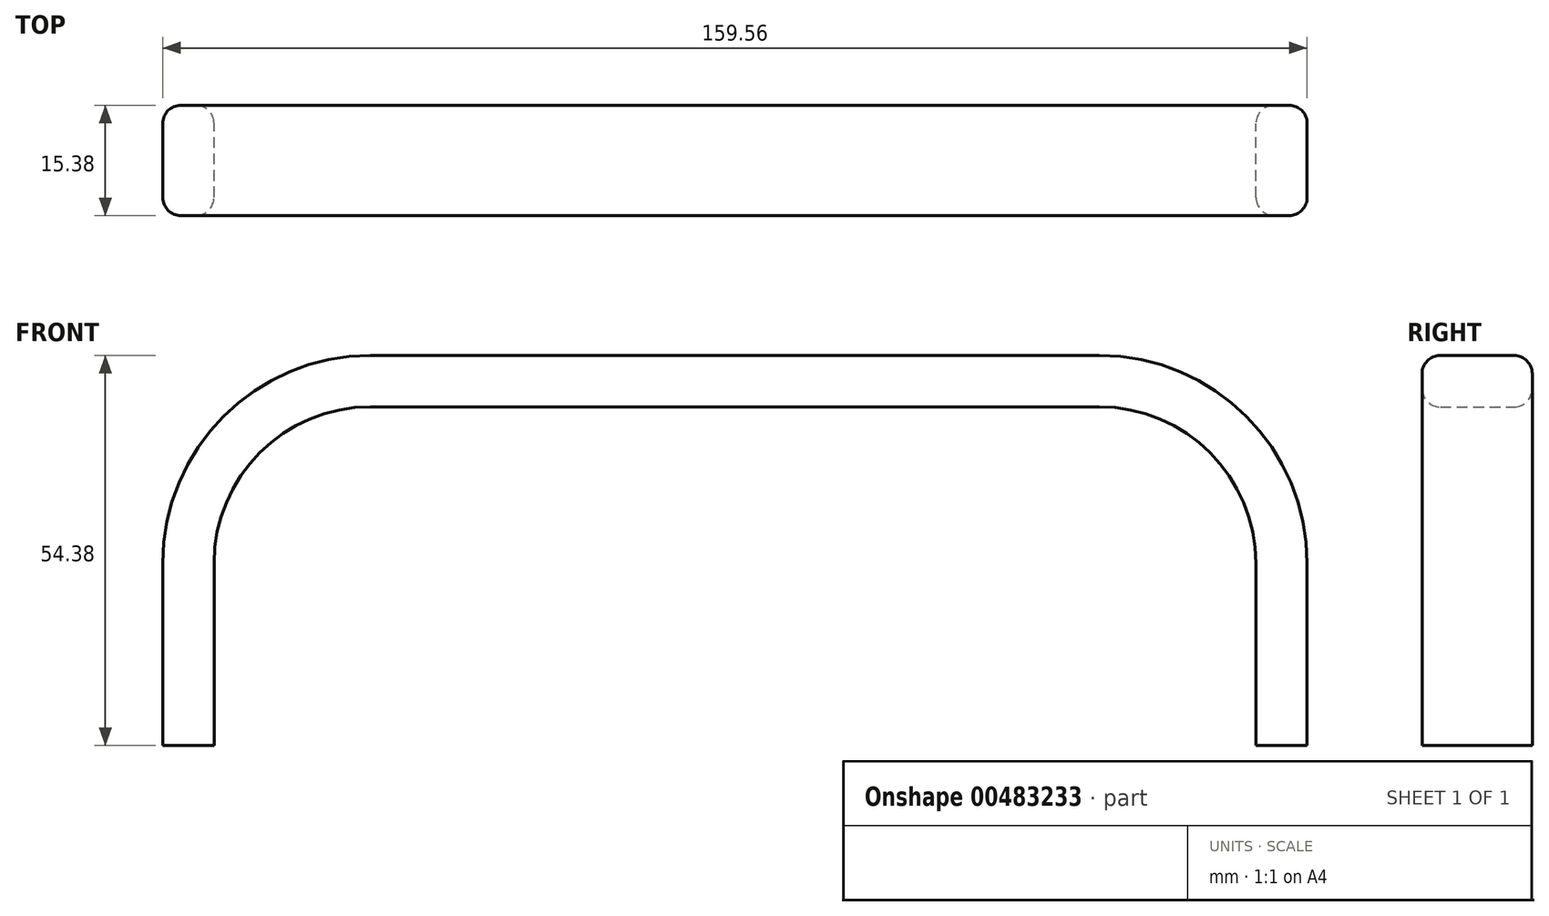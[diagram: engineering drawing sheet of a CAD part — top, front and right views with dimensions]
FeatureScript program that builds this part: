
annotation { "Feature Type Name" : "Feature", "Feature Type Description" : "" }
export const myFeature = defineFeature(function(context is Context, id is Id, definition is map)
    precondition{}
    {
        {
            var Q0;
            Q0=qCreatedBy(makeId("Front.planeOp"),FACE);
            var sketch = newSketch(context, id + "F0", { "sketchPlane" : qUnion([Q0])});
            skLineSegment(sketch, "E0", {"start": v(-76.2, 0) * mm, "end": v(-76.2, 25.4) * mm});
            skLineSegment(sketch, "E1", {"start": v(-50.8, 50.8) * mm, "end": v(50.8, 50.8) * mm});
            skLineSegment(sketch, "E2", {"start": v(76.2, 25.4) * mm, "end": v(76.2, 0) * mm});
            skPoint(sketch, "E3.visualSharp", {"position": v(-76.2, 50.8) * mm});
            skArc(sketch, "E3.filletArc", {"start": v(-50.8, 50.8) * mm, "mid": v(-68.76, 43.36) * mm, "end": v(-76.2, 25.4) * mm});
            skPoint(sketch, "E4.visualSharp", {"position": v(76.2, 50.8) * mm});
            skArc(sketch, "E4.filletArc", {"start": v(76.2, 25.4) * mm, "mid": v(68.76, 43.36) * mm, "end": v(50.8, 50.8) * mm});
            skSolve(sketch);
        }
        {
            var Q0;
            Q0=qCreatedBy(makeId("Top.planeOp"),FACE);
            var sketch = newSketch(context, id + "F1", { "sketchPlane" : qUnion([Q0])});
            skLineSegment(sketch, "E5.bottom", {"start": v(-75.16, -7.69) * mm, "end": v(-77.24, -7.69) * mm});
            skLineSegment(sketch, "E5.top", {"start": v(-75.16, 7.69) * mm, "end": v(-77.24, 7.69) * mm});
            skLineSegment(sketch, "E5.left", {"start": v(-72.62, -5.15) * mm, "end": v(-72.62, 5.15) * mm});
            skLineSegment(sketch, "E5.right", {"start": v(-79.78, -5.15) * mm, "end": v(-79.78, 5.15) * mm});
            skPoint(sketch, "E5.middle", {"position": v(-76.2, 0) * mm});
            skPoint(sketch, "E6.visualSharp", {"position": v(-79.78, -7.69) * mm});
            skArc(sketch, "E6.filletArc", {"start": v(-79.78, -5.15) * mm, "mid": v(-79.04, -6.94) * mm, "end": v(-77.24, -7.69) * mm});
            skPoint(sketch, "E7.visualSharp", {"position": v(-72.62, -7.69) * mm});
            skArc(sketch, "E7.filletArc", {"start": v(-75.16, -7.69) * mm, "mid": v(-73.36, -6.94) * mm, "end": v(-72.62, -5.15) * mm});
            skPoint(sketch, "E8.visualSharp", {"position": v(-72.62, 7.69) * mm});
            skArc(sketch, "E8.filletArc", {"start": v(-72.62, 5.15) * mm, "mid": v(-73.36, 6.94) * mm, "end": v(-75.16, 7.69) * mm});
            skPoint(sketch, "E9.visualSharp", {"position": v(-79.78, 7.69) * mm});
            skArc(sketch, "E9.filletArc", {"start": v(-77.24, 7.69) * mm, "mid": v(-79.04, 6.94) * mm, "end": v(-79.78, 5.15) * mm});
            skSolve(sketch);
        }
        {
            var Q0;
            Q0 = qSketchRegion(id + "F1", true);
            var Q1;
            Q1=sQuery(id+"F0.wireOp",EDGE,"E0");
            var Q2;
            Q2=sQuery(id+"F0.wireOp",EDGE,"E3.filletArc");
            var Q3;
            Q3=sQuery(id+"F0.wireOp",EDGE,"E1");
            var Q4;
            Q4=sQuery(id+"F0.wireOp",EDGE,"E4.filletArc");
            var Q5;
            Q5=sQuery(id+"F0.wireOp",EDGE,"E2");
            sweep(context, id + "F2", {"profiles" : qUnion([Q0]), "path" : qUnion([Q1, Q2, Q3, Q4, Q5])});
        }
    });
